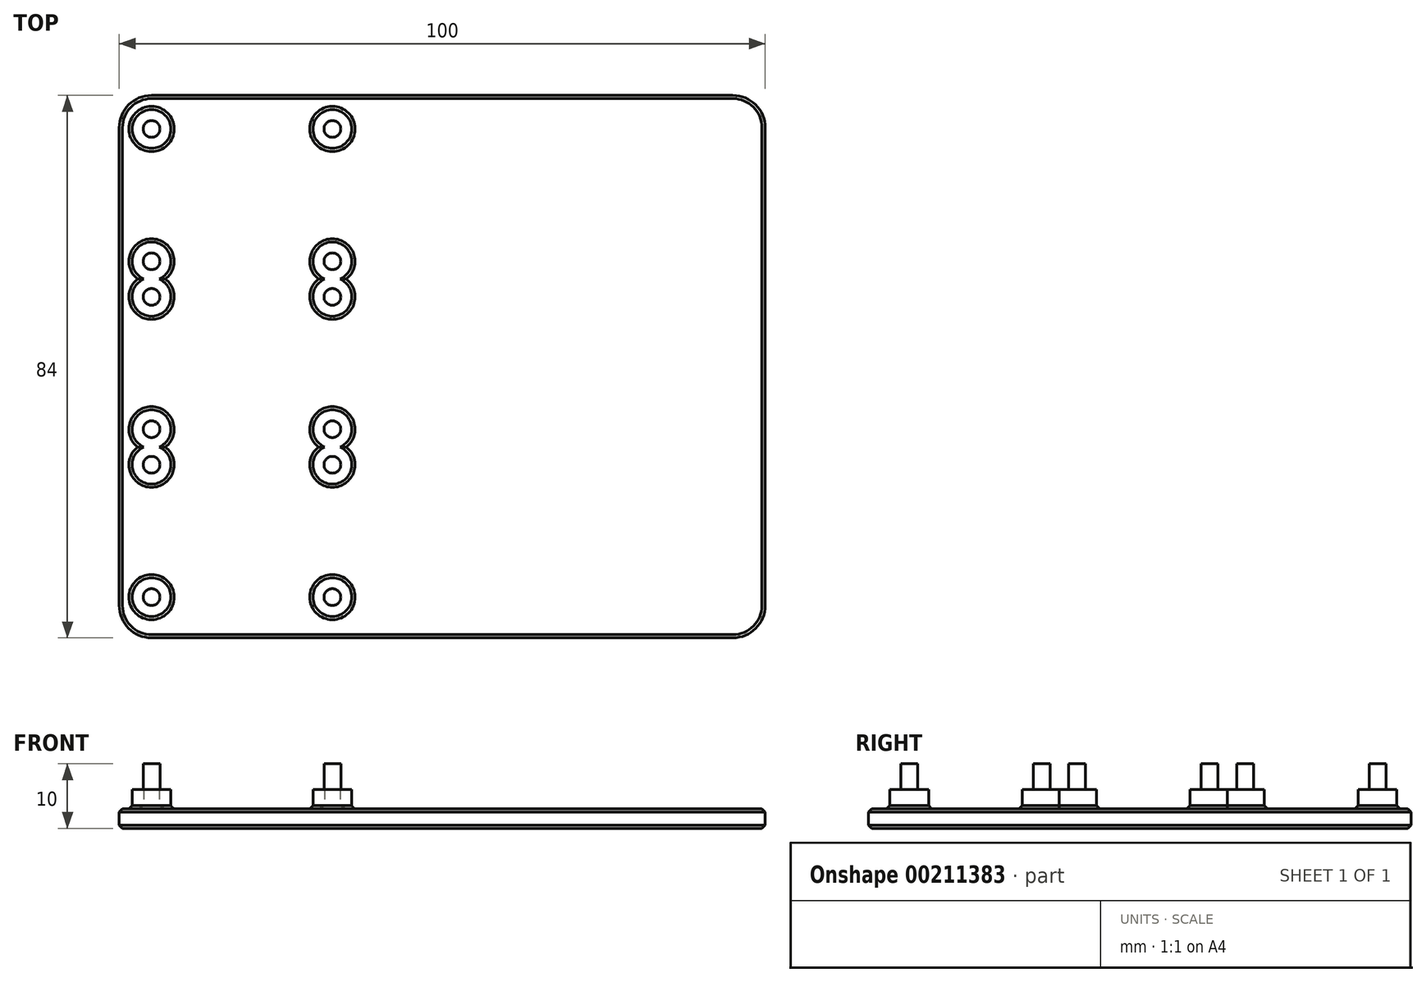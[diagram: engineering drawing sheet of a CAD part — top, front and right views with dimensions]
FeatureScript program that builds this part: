
annotation { "Feature Type Name" : "Feature", "Feature Type Description" : "" }
export const myFeature = defineFeature(function(context is Context, id is Id, definition is map)
    precondition{}
    {
        {
            var Q0;
            Q0=qCreatedBy(makeId("Top.planeOp"),FACE);
            var sketch = newSketch(context, id + "F0", { "sketchPlane" : qUnion([Q0])});
            skLineSegment(sketch, "E0.bottom", {"start": v(-97.44, 60.47) * mm, "end": v(2.56, 60.47) * mm});
            skLineSegment(sketch, "E0.top", {"start": v(-97.44, -23.53) * mm, "end": v(2.56, -23.53) * mm});
            skLineSegment(sketch, "E0.left", {"start": v(-97.44, 60.47) * mm, "end": v(-97.44, -23.53) * mm});
            skLineSegment(sketch, "E0.right", {"start": v(2.56, 60.47) * mm, "end": v(2.56, -23.53) * mm});
            skCircle(sketch, "E1", {"center": v(-92.44, 55.27) * mm, "radius": 1.3 * mm});
            skCircle(sketch, "E2", {"center": v(-64.44, 55.27) * mm, "radius": 1.3 * mm});
            skCircle(sketch, "E3", {"center": v(-92.44, 34.77) * mm, "radius": 1.3 * mm});
            skCircle(sketch, "E4", {"center": v(-64.44, 34.77) * mm, "radius": 1.3 * mm});
            skCircle(sketch, "E5", {"center": v(-92.44, 29.27) * mm, "radius": 1.3 * mm});
            skCircle(sketch, "E6", {"center": v(-64.44, 29.27) * mm, "radius": 1.3 * mm});
            skCircle(sketch, "E7", {"center": v(-92.44, 8.77) * mm, "radius": 1.3 * mm});
            skCircle(sketch, "E8", {"center": v(-64.44, 8.77) * mm, "radius": 1.3 * mm});
            skCircle(sketch, "E9", {"center": v(-92.44, 3.27) * mm, "radius": 1.3 * mm});
            skCircle(sketch, "E10", {"center": v(-64.44, 3.27) * mm, "radius": 1.3 * mm});
            skCircle(sketch, "E11", {"center": v(-92.44, -17.23) * mm, "radius": 1.3 * mm});
            skCircle(sketch, "E12", {"center": v(-64.44, -17.23) * mm, "radius": 1.3 * mm});
            skCircle(sketch, "E13", {"center": v(-92.44, 55.27) * mm, "radius": 3 * mm});
            skCircle(sketch, "E14", {"center": v(-64.44, 55.27) * mm, "radius": 3 * mm});
            skCircle(sketch, "E15", {"center": v(-64.44, 34.77) * mm, "radius": 3 * mm});
            skCircle(sketch, "E16", {"center": v(-64.44, 29.27) * mm, "radius": 3 * mm});
            skCircle(sketch, "E17", {"center": v(-92.44, 34.77) * mm, "radius": 3 * mm});
            skCircle(sketch, "E18", {"center": v(-92.44, 29.27) * mm, "radius": 3 * mm});
            skCircle(sketch, "E19", {"center": v(-92.44, 8.77) * mm, "radius": 3 * mm});
            skCircle(sketch, "E20", {"center": v(-92.44, 3.27) * mm, "radius": 3 * mm});
            skCircle(sketch, "E21", {"center": v(-92.44, -17.23) * mm, "radius": 3 * mm});
            skCircle(sketch, "E22", {"center": v(-64.44, 8.77) * mm, "radius": 3 * mm});
            skCircle(sketch, "E23", {"center": v(-64.44, 3.27) * mm, "radius": 3 * mm});
            skCircle(sketch, "E24", {"center": v(-64.44, -17.23) * mm, "radius": 3 * mm});
            skSolve(sketch);
        }
        {
            var Q0;
            Q0=makeQuery(id+"F0.imprint","IMPRINT",FACE,{"disambiguationData":[TD([[makeQuery(id+"F0.imprint","IMPRINT",EDGE,{"derivedFrom":sQuery(id+"F0.wireOp",EDGE,"E1")}),1.0]])]});
            var Q1;
            Q1=makeQuery(id+"F0.imprint","IMPRINT",FACE,{"disambiguationData":[TD([[makeQuery(id+"F0.imprint","IMPRINT",EDGE,{"derivedFrom":sQuery(id+"F0.wireOp",EDGE,"E2")}),1.0]])]});
            var Q2;
            Q2=makeQuery(id+"F0.imprint","IMPRINT",FACE,{"disambiguationData":[TD([[makeQuery(id+"F0.imprint","IMPRINT",EDGE,{"derivedFrom":sQuery(id+"F0.wireOp",EDGE,"E4")}),1.0]])]});
            var Q3;
            Q3=makeQuery(id+"F0.imprint","IMPRINT",FACE,{"disambiguationData":[TD([[makeQuery(id+"F0.imprint","IMPRINT",EDGE,{"derivedFrom":sQuery(id+"F0.wireOp",EDGE,"E6")}),1.0]])]});
            var Q4;
            Q4=makeQuery(id+"F0.imprint","IMPRINT",FACE,{"disambiguationData":[TD([[makeQuery(id+"F0.imprint","IMPRINT",EDGE,{"derivedFrom":sQuery(id+"F0.wireOp",EDGE,"E8")}),1.0]])]});
            var Q5;
            Q5=makeQuery(id+"F0.imprint","IMPRINT",FACE,{"disambiguationData":[TD([[makeQuery(id+"F0.imprint","IMPRINT",EDGE,{"derivedFrom":sQuery(id+"F0.wireOp",EDGE,"E10")}),1.0]])]});
            var Q6;
            Q6=makeQuery(id+"F0.imprint","IMPRINT",FACE,{"disambiguationData":[TD([[makeQuery(id+"F0.imprint","IMPRINT",EDGE,{"derivedFrom":sQuery(id+"F0.wireOp",EDGE,"E12")}),1.0]])]});
            var Q7;
            Q7=makeQuery(id+"F0.imprint","IMPRINT",FACE,{"disambiguationData":[TD([[makeQuery(id+"F0.imprint","IMPRINT",EDGE,{"derivedFrom":sQuery(id+"F0.wireOp",EDGE,"E11")}),1.0]])]});
            var Q8;
            Q8=makeQuery(id+"F0.imprint","IMPRINT",FACE,{"disambiguationData":[TD([[makeQuery(id+"F0.imprint","IMPRINT",EDGE,{"derivedFrom":sQuery(id+"F0.wireOp",EDGE,"E9")}),1.0]])]});
            var Q9;
            Q9=makeQuery(id+"F0.imprint","IMPRINT",FACE,{"disambiguationData":[TD([[makeQuery(id+"F0.imprint","IMPRINT",EDGE,{"derivedFrom":sQuery(id+"F0.wireOp",EDGE,"E7")}),1.0]])]});
            var Q10;
            Q10=makeQuery(id+"F0.imprint","IMPRINT",FACE,{"disambiguationData":[TD([[makeQuery(id+"F0.imprint","IMPRINT",EDGE,{"derivedFrom":sQuery(id+"F0.wireOp",EDGE,"E5")}),1.0]])]});
            var Q11;
            Q11=makeQuery(id+"F0.imprint","IMPRINT",FACE,{"disambiguationData":[TD([[makeQuery(id+"F0.imprint","IMPRINT",EDGE,{"derivedFrom":sQuery(id+"F0.wireOp",EDGE,"E3")}),1.0]])]});
            extrude(context, id + "F1", {"entities" : qUnion([Q0, Q1, Q2, Q3, Q4, Q5, Q6, Q7, Q8, Q9, Q10, Q11]), "depth" : 10 * mm, "offsetDistance" : 25 * mm});
        }
        {
            var Q0;
            Q0=makeQuery(id+"F0.imprint","IMPRINT",FACE,{"disambiguationData":[TD([[makeQuery(id+"F0.imprint","IMPRINT",EDGE,{"derivedFrom":sQuery(id+"F0.wireOp",EDGE,"E1")}),-1.0]])]});
            var Q1;
            Q1=makeQuery(id+"F0.imprint","IMPRINT",FACE,{"disambiguationData":[TD([[makeQuery(id+"F0.imprint","IMPRINT",EDGE,{"derivedFrom":sQuery(id+"F0.wireOp",EDGE,"E2")}),-1.0]])]});
            var Q2;
            Q2=makeQuery(id+"F0.imprint","IMPRINT",FACE,{"disambiguationData":[TD([[makeQuery(id+"F0.imprint","IMPRINT",EDGE,{"derivedFrom":sQuery(id+"F0.wireOp",EDGE,"E4")}),-1.0]])]});
            var Q3;
            Q3=makeQuery(id+"F0.imprint","IMPRINT",FACE,{"disambiguationData":[TD([[makeQuery(id+"F0.imprint","IMPRINT",EDGE,{"derivedFrom":sQuery(id+"F0.wireOp",EDGE,"E6")}),-1.0]])]});
            var Q4;
            Q4=makeQuery(id+"F0.imprint","IMPRINT",FACE,{"disambiguationData":[TD([[makeQuery(id+"F0.imprint","IMPRINT",EDGE,{"derivedFrom":sQuery(id+"F0.wireOp",EDGE,"E8")}),-1.0]])]});
            var Q5;
            Q5=makeQuery(id+"F0.imprint","IMPRINT",FACE,{"disambiguationData":[TD([[makeQuery(id+"F0.imprint","IMPRINT",EDGE,{"derivedFrom":sQuery(id+"F0.wireOp",EDGE,"E10")}),-1.0]])]});
            var Q6;
            Q6=makeQuery(id+"F0.imprint","IMPRINT",FACE,{"disambiguationData":[TD([[makeQuery(id+"F0.imprint","IMPRINT",EDGE,{"derivedFrom":sQuery(id+"F0.wireOp",EDGE,"E12")}),-1.0]])]});
            var Q7;
            Q7=makeQuery(id+"F0.imprint","IMPRINT",FACE,{"disambiguationData":[TD([[makeQuery(id+"F0.imprint","IMPRINT",EDGE,{"derivedFrom":sQuery(id+"F0.wireOp",EDGE,"E11")}),-1.0]])]});
            var Q8;
            Q8=makeQuery(id+"F0.imprint","IMPRINT",FACE,{"disambiguationData":[TD([[makeQuery(id+"F0.imprint","IMPRINT",EDGE,{"derivedFrom":sQuery(id+"F0.wireOp",EDGE,"E9")}),-1.0]])]});
            var Q9;
            Q9=makeQuery(id+"F0.imprint","IMPRINT",FACE,{"disambiguationData":[TD([[makeQuery(id+"F0.imprint","IMPRINT",EDGE,{"derivedFrom":sQuery(id+"F0.wireOp",EDGE,"E7")}),-1.0]])]});
            var Q10;
            Q10=makeQuery(id+"F0.imprint","IMPRINT",FACE,{"disambiguationData":[TD([[makeQuery(id+"F0.imprint","IMPRINT",EDGE,{"derivedFrom":sQuery(id+"F0.wireOp",EDGE,"E5")}),-1.0]])]});
            var Q11;
            Q11=makeQuery(id+"F0.imprint","IMPRINT",FACE,{"disambiguationData":[TD([[makeQuery(id+"F0.imprint","IMPRINT",EDGE,{"derivedFrom":sQuery(id+"F0.wireOp",EDGE,"E3")}),-1.0]])]});
            var Q12;
            {var subQ0=sQuery(id+"F0.wireOp",EDGE,"E18");var subQ1=sQuery(id+"F0.wireOp",EDGE,"E17");var subQ2=makeQuery(id+"F0.imprint","INTERSECT",VERTEX,{"disambiguationData":[OD(0.0)],"derivedFrom":[subQ1,subQ0]});Q12=makeQuery(id+"F0.imprint","IMPRINT",FACE,{"disambiguationData":[TD([[makeQuery(id+"F0.imprint","IMPRINT",EDGE,{"disambiguationData":[TD([[subQ2,-1.0]])],"derivedFrom":subQ1}),1.0]])]});}
            var Q13;
            {var subQ0=sQuery(id+"F0.wireOp",EDGE,"E16");var subQ1=sQuery(id+"F0.wireOp",EDGE,"E15");var subQ2=makeQuery(id+"F0.imprint","INTERSECT",VERTEX,{"disambiguationData":[OD(0.0)],"derivedFrom":[subQ1,subQ0]});Q13=makeQuery(id+"F0.imprint","IMPRINT",FACE,{"disambiguationData":[TD([[makeQuery(id+"F0.imprint","IMPRINT",EDGE,{"disambiguationData":[TD([[subQ2,-1.0]])],"derivedFrom":subQ1}),1.0]])]});}
            var Q14;
            {var subQ0=sQuery(id+"F0.wireOp",EDGE,"E23");var subQ1=sQuery(id+"F0.wireOp",EDGE,"E22");var subQ2=makeQuery(id+"F0.imprint","INTERSECT",VERTEX,{"disambiguationData":[OD(0.0)],"derivedFrom":[subQ1,subQ0]});Q14=makeQuery(id+"F0.imprint","IMPRINT",FACE,{"disambiguationData":[TD([[makeQuery(id+"F0.imprint","IMPRINT",EDGE,{"disambiguationData":[TD([[subQ2,-1.0]])],"derivedFrom":subQ1}),1.0]])]});}
            var Q15;
            {var subQ0=sQuery(id+"F0.wireOp",EDGE,"E20");var subQ1=sQuery(id+"F0.wireOp",EDGE,"E19");var subQ2=makeQuery(id+"F0.imprint","INTERSECT",VERTEX,{"disambiguationData":[OD(0.0)],"derivedFrom":[subQ1,subQ0]});Q15=makeQuery(id+"F0.imprint","IMPRINT",FACE,{"disambiguationData":[TD([[makeQuery(id+"F0.imprint","IMPRINT",EDGE,{"disambiguationData":[TD([[subQ2,-1.0]])],"derivedFrom":subQ1}),1.0]])]});}
            extrude(context, id + "F2", {"entities" : qUnion([Q0, Q1, Q2, Q3, Q4, Q5, Q6, Q7, Q8, Q9, Q10, Q11, Q12, Q13, Q14, Q15]), "depth" : 6 * mm, "offsetDistance" : 25 * mm});
        }
        {
            var Q0;
            Q0=makeQuery(id+"F0.imprint","IMPRINT",FACE,{"disambiguationData":[TD([[makeQuery(id+"F0.imprint","IMPRINT",EDGE,{"derivedFrom":sQuery(id+"F0.wireOp",EDGE,"E0.bottom")}),-1.0]])]});
            extrude(context, id + "F3", {"entities" : qUnion([Q0]), "depth" : 3 * mm, "offsetDistance" : 25 * mm});
        }
        {
            var Q0;
            Q0=makeQuery(id+"F3.opExtrude","SWEPT_BODY",BODY,{"disambiguationData":[OSD([sQuery(id+"F0.wireOp",EDGE,"E0.bottom"),sQuery(id+"F0.wireOp",EDGE,"E0.top"),sQuery(id+"F0.wireOp",EDGE,"E0.left"),sQuery(id+"F0.wireOp",EDGE,"E0.right"),sQuery(id+"F0.wireOp",EDGE,"E13"),sQuery(id+"F0.wireOp",EDGE,"E14"),sQuery(id+"F0.wireOp",EDGE,"E15"),sQuery(id+"F0.wireOp",EDGE,"E16"),sQuery(id+"F0.wireOp",EDGE,"E17"),sQuery(id+"F0.wireOp",EDGE,"E18"),sQuery(id+"F0.wireOp",EDGE,"E19"),sQuery(id+"F0.wireOp",EDGE,"E20"),sQuery(id+"F0.wireOp",EDGE,"E21"),sQuery(id+"F0.wireOp",EDGE,"E22"),sQuery(id+"F0.wireOp",EDGE,"E23"),sQuery(id+"F0.wireOp",EDGE,"E24")])]});
            var Q1;
            Q1=makeQuery(id+"F2.opExtrude","SWEPT_BODY",BODY,{"disambiguationData":[OSD([sQuery(id+"F0.wireOp",EDGE,"E1"),sQuery(id+"F0.wireOp",EDGE,"E13")])]});
            var Q2;
            Q2=makeQuery(id+"F2.opExtrude","SWEPT_BODY",BODY,{"disambiguationData":[OSD([sQuery(id+"F0.wireOp",EDGE,"E3"),sQuery(id+"F0.wireOp",EDGE,"E5"),sQuery(id+"F0.wireOp",EDGE,"E17"),sQuery(id+"F0.wireOp",EDGE,"E18")])]});
            var Q3;
            Q3=makeQuery(id+"F2.opExtrude","SWEPT_BODY",BODY,{"disambiguationData":[OSD([sQuery(id+"F0.wireOp",EDGE,"E2"),sQuery(id+"F0.wireOp",EDGE,"E14")])]});
            var Q4;
            Q4=makeQuery(id+"F2.opExtrude","SWEPT_BODY",BODY,{"disambiguationData":[OSD([sQuery(id+"F0.wireOp",EDGE,"E4"),sQuery(id+"F0.wireOp",EDGE,"E6"),sQuery(id+"F0.wireOp",EDGE,"E15"),sQuery(id+"F0.wireOp",EDGE,"E16")])]});
            var Q5;
            Q5=makeQuery(id+"F2.opExtrude","SWEPT_BODY",BODY,{"disambiguationData":[OSD([sQuery(id+"F0.wireOp",EDGE,"E7"),sQuery(id+"F0.wireOp",EDGE,"E9"),sQuery(id+"F0.wireOp",EDGE,"E19"),sQuery(id+"F0.wireOp",EDGE,"E20")])]});
            var Q6;
            Q6=makeQuery(id+"F2.opExtrude","SWEPT_BODY",BODY,{"disambiguationData":[OSD([sQuery(id+"F0.wireOp",EDGE,"E8"),sQuery(id+"F0.wireOp",EDGE,"E10"),sQuery(id+"F0.wireOp",EDGE,"E22"),sQuery(id+"F0.wireOp",EDGE,"E23")])]});
            var Q7;
            Q7=makeQuery(id+"F2.opExtrude","SWEPT_BODY",BODY,{"disambiguationData":[OSD([sQuery(id+"F0.wireOp",EDGE,"E11"),sQuery(id+"F0.wireOp",EDGE,"E21")])]});
            var Q8;
            Q8=makeQuery(id+"F2.opExtrude","SWEPT_BODY",BODY,{"disambiguationData":[OSD([sQuery(id+"F0.wireOp",EDGE,"E12"),sQuery(id+"F0.wireOp",EDGE,"E24")])]});
            var Q9;
            Q9=makeQuery(id+"F1.opExtrude","SWEPT_BODY",BODY,{"disambiguationData":[OSD([sQuery(id+"F0.wireOp",EDGE,"E1")])]});
            var Q10;
            Q10=makeQuery(id+"F1.opExtrude","SWEPT_BODY",BODY,{"disambiguationData":[OSD([sQuery(id+"F0.wireOp",EDGE,"E3")])]});
            var Q11;
            Q11=makeQuery(id+"F1.opExtrude","SWEPT_BODY",BODY,{"disambiguationData":[OSD([sQuery(id+"F0.wireOp",EDGE,"E2")])]});
            var Q12;
            Q12=makeQuery(id+"F1.opExtrude","SWEPT_BODY",BODY,{"disambiguationData":[OSD([sQuery(id+"F0.wireOp",EDGE,"E4")])]});
            var Q13;
            Q13=makeQuery(id+"F1.opExtrude","SWEPT_BODY",BODY,{"disambiguationData":[OSD([sQuery(id+"F0.wireOp",EDGE,"E5")])]});
            var Q14;
            Q14=makeQuery(id+"F1.opExtrude","SWEPT_BODY",BODY,{"disambiguationData":[OSD([sQuery(id+"F0.wireOp",EDGE,"E6")])]});
            var Q15;
            Q15=makeQuery(id+"F1.opExtrude","SWEPT_BODY",BODY,{"disambiguationData":[OSD([sQuery(id+"F0.wireOp",EDGE,"E7")])]});
            var Q16;
            Q16=makeQuery(id+"F1.opExtrude","SWEPT_BODY",BODY,{"disambiguationData":[OSD([sQuery(id+"F0.wireOp",EDGE,"E8")])]});
            var Q17;
            Q17=makeQuery(id+"F1.opExtrude","SWEPT_BODY",BODY,{"disambiguationData":[OSD([sQuery(id+"F0.wireOp",EDGE,"E9")])]});
            var Q18;
            Q18=makeQuery(id+"F1.opExtrude","SWEPT_BODY",BODY,{"disambiguationData":[OSD([sQuery(id+"F0.wireOp",EDGE,"E10")])]});
            var Q19;
            Q19=makeQuery(id+"F1.opExtrude","SWEPT_BODY",BODY,{"disambiguationData":[OSD([sQuery(id+"F0.wireOp",EDGE,"E11")])]});
            var Q20;
            Q20=makeQuery(id+"F1.opExtrude","SWEPT_BODY",BODY,{"disambiguationData":[OSD([sQuery(id+"F0.wireOp",EDGE,"E12")])]});
            booleanBodies(context, id + "F4", {"operationType" : BooleanOperationType.UNION, "tools" : qUnion([Q0, Q1, Q2, Q3, Q4, Q5, Q6, Q7, Q8, Q9, Q10, Q11, Q12, Q13, Q14, Q15, Q16, Q17, Q18, Q19, Q20])});
        }
        {
            var Q0;
            Q0=makeQuery(id+"F3.opExtrude","SWEPT_EDGE",EDGE,{"disambiguationData":[OSD([sQuery(id+"F0.wireOp",EDGE,"E0.top"),sQuery(id+"F0.wireOp",EDGE,"E0.left")])]});
            var Q1;
            Q1=makeQuery(id+"F3.opExtrude","SWEPT_EDGE",EDGE,{"disambiguationData":[OSD([sQuery(id+"F0.wireOp",EDGE,"E0.top"),sQuery(id+"F0.wireOp",EDGE,"E0.right")])]});
            var Q2;
            Q2=makeQuery(id+"F3.opExtrude","SWEPT_EDGE",EDGE,{"disambiguationData":[OSD([sQuery(id+"F0.wireOp",EDGE,"E0.bottom"),sQuery(id+"F0.wireOp",EDGE,"E0.right")])]});
            var Q3;
            Q3=makeQuery(id+"F3.opExtrude","SWEPT_EDGE",EDGE,{"disambiguationData":[OSD([sQuery(id+"F0.wireOp",EDGE,"E0.bottom"),sQuery(id+"F0.wireOp",EDGE,"E0.left")])]});
            fillet(context, id + "F5", {"entities" : qUnion([Q0, Q1, Q2, Q3]), "tangentPropagation" : true, "radius" : 5 * mm, "defaultsChanged" : false, "vertexSettings" : [], "allowEdgeOverflow" : false});
        }
        {
            var Q0;
            {var subQ0=sQuery(id+"F0.wireOp",EDGE,"E24");var subQ1=sQuery(id+"F0.wireOp",EDGE,"E23");var subQ2=sQuery(id+"F0.wireOp",EDGE,"E22");var subQ3=sQuery(id+"F0.wireOp",EDGE,"E21");var subQ4=sQuery(id+"F0.wireOp",EDGE,"E20");var subQ5=sQuery(id+"F0.wireOp",EDGE,"E19");var subQ6=sQuery(id+"F0.wireOp",EDGE,"E18");var subQ7=sQuery(id+"F0.wireOp",EDGE,"E17");var subQ8=sQuery(id+"F0.wireOp",EDGE,"E16");var subQ9=sQuery(id+"F0.wireOp",EDGE,"E15");var subQ10=sQuery(id+"F0.wireOp",EDGE,"E14");var subQ11=sQuery(id+"F0.wireOp",EDGE,"E13");var subQ12=sQuery(id+"F0.wireOp",EDGE,"E12");var subQ13=sQuery(id+"F0.wireOp",EDGE,"E11");var subQ14=sQuery(id+"F0.wireOp",EDGE,"E10");var subQ15=sQuery(id+"F0.wireOp",EDGE,"E8");var subQ16=sQuery(id+"F0.wireOp",EDGE,"E9");var subQ17=sQuery(id+"F0.wireOp",EDGE,"E7");var subQ18=sQuery(id+"F0.wireOp",EDGE,"E6");var subQ19=sQuery(id+"F0.wireOp",EDGE,"E4");var subQ20=sQuery(id+"F0.wireOp",EDGE,"E5");var subQ21=sQuery(id+"F0.wireOp",EDGE,"E3");var subQ22=sQuery(id+"F0.wireOp",EDGE,"E2");var subQ23=sQuery(id+"F0.wireOp",EDGE,"E1");Q0=makeQuery(id+"F4.opBoolean","MERGE",FACE,{"derivedFrom":[makeQuery(id+"F1.opExtrude","CAP_FACE",FACE,{"disambiguationData":[OSD([subQ23])],"isStart":true}),makeQuery(id+"F1.opExtrude","CAP_FACE",FACE,{"disambiguationData":[OSD([subQ22])],"isStart":true}),makeQuery(id+"F1.opExtrude","CAP_FACE",FACE,{"disambiguationData":[OSD([subQ21])],"isStart":true}),makeQuery(id+"F1.opExtrude","CAP_FACE",FACE,{"disambiguationData":[OSD([subQ19])],"isStart":true}),makeQuery(id+"F1.opExtrude","CAP_FACE",FACE,{"disambiguationData":[OSD([subQ20])],"isStart":true}),makeQuery(id+"F1.opExtrude","CAP_FACE",FACE,{"disambiguationData":[OSD([subQ18])],"isStart":true}),makeQuery(id+"F1.opExtrude","CAP_FACE",FACE,{"disambiguationData":[OSD([subQ17])],"isStart":true}),makeQuery(id+"F1.opExtrude","CAP_FACE",FACE,{"disambiguationData":[OSD([subQ15])],"isStart":true}),makeQuery(id+"F1.opExtrude","CAP_FACE",FACE,{"disambiguationData":[OSD([subQ16])],"isStart":true}),makeQuery(id+"F1.opExtrude","CAP_FACE",FACE,{"disambiguationData":[OSD([subQ14])],"isStart":true}),makeQuery(id+"F1.opExtrude","CAP_FACE",FACE,{"disambiguationData":[OSD([subQ13])],"isStart":true}),makeQuery(id+"F1.opExtrude","CAP_FACE",FACE,{"disambiguationData":[OSD([subQ12])],"isStart":true}),makeQuery(id+"F2.opExtrude","CAP_FACE",FACE,{"disambiguationData":[OSD([subQ23,subQ11])],"isStart":true}),makeQuery(id+"F2.opExtrude","CAP_FACE",FACE,{"disambiguationData":[OSD([subQ22,subQ10])],"isStart":true}),makeQuery(id+"F2.opExtrude","CAP_FACE",FACE,{"disambiguationData":[OSD([subQ21,subQ20,subQ7,subQ6])],"isStart":true}),makeQuery(id+"F2.opExtrude","CAP_FACE",FACE,{"disambiguationData":[OSD([subQ19,subQ18,subQ9,subQ8])],"isStart":true}),makeQuery(id+"F2.opExtrude","CAP_FACE",FACE,{"disambiguationData":[OSD([subQ17,subQ16,subQ5,subQ4])],"isStart":true}),makeQuery(id+"F2.opExtrude","CAP_FACE",FACE,{"disambiguationData":[OSD([subQ15,subQ14,subQ2,subQ1])],"isStart":true}),makeQuery(id+"F2.opExtrude","CAP_FACE",FACE,{"disambiguationData":[OSD([subQ13,subQ3])],"isStart":true}),makeQuery(id+"F2.opExtrude","CAP_FACE",FACE,{"disambiguationData":[OSD([subQ12,subQ0])],"isStart":true}),makeQuery(id+"F3.opExtrude","CAP_FACE",FACE,{"disambiguationData":[OSD([sQuery(id+"F0.wireOp",EDGE,"E0.bottom"),sQuery(id+"F0.wireOp",EDGE,"E0.top"),sQuery(id+"F0.wireOp",EDGE,"E0.left"),sQuery(id+"F0.wireOp",EDGE,"E0.right"),subQ11,subQ10,subQ9,subQ8,subQ7,subQ6,subQ5,subQ4,subQ3,subQ2,subQ1,subQ0])],"isStart":true})]});}
            chamfer(context, id + "F6", {"entities" : qUnion([Q0]), "width" : .5 * mm, "tangentPropagation" : true});
        }
        {
            var Q0;
            Q0=makeQuery(id+"F3.opExtrude","CAP_FACE",FACE,{"disambiguationData":[OSD([sQuery(id+"F0.wireOp",EDGE,"E0.bottom"),sQuery(id+"F0.wireOp",EDGE,"E0.top"),sQuery(id+"F0.wireOp",EDGE,"E0.left"),sQuery(id+"F0.wireOp",EDGE,"E0.right"),sQuery(id+"F0.wireOp",EDGE,"E13"),sQuery(id+"F0.wireOp",EDGE,"E14"),sQuery(id+"F0.wireOp",EDGE,"E15"),sQuery(id+"F0.wireOp",EDGE,"E16"),sQuery(id+"F0.wireOp",EDGE,"E17"),sQuery(id+"F0.wireOp",EDGE,"E18"),sQuery(id+"F0.wireOp",EDGE,"E19"),sQuery(id+"F0.wireOp",EDGE,"E20"),sQuery(id+"F0.wireOp",EDGE,"E21"),sQuery(id+"F0.wireOp",EDGE,"E22"),sQuery(id+"F0.wireOp",EDGE,"E23"),sQuery(id+"F0.wireOp",EDGE,"E24")])],"isStart":false});
            chamfer(context, id + "F7", {"entities" : qUnion([Q0]), "width" : .5 * mm, "tangentPropagation" : true});
        }
    });
